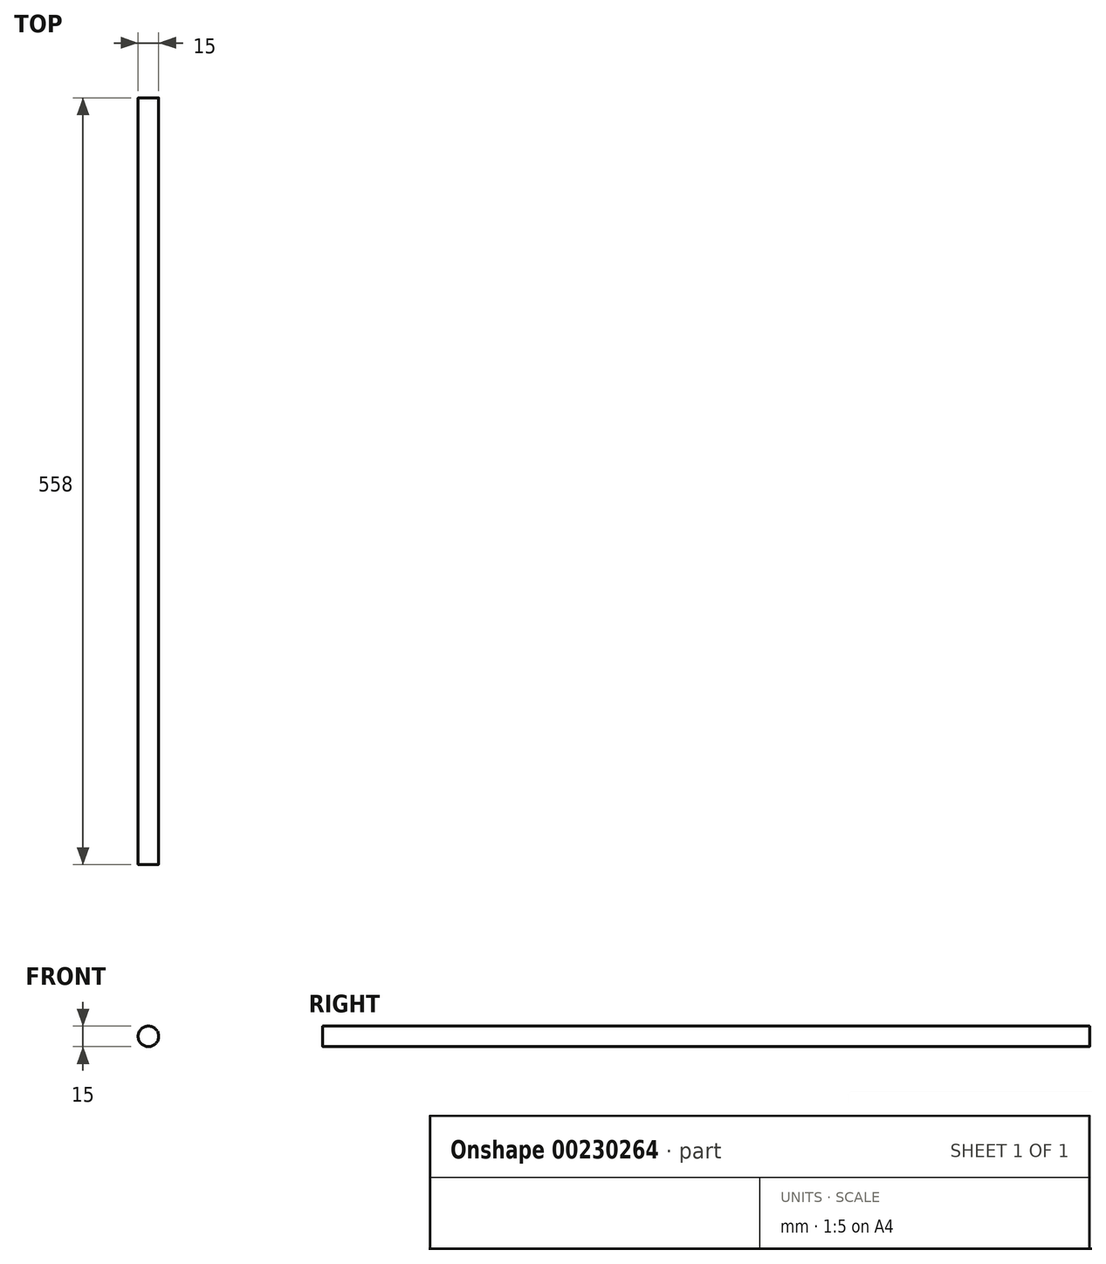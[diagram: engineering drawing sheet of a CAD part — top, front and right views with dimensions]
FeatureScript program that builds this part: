
annotation { "Feature Type Name" : "Feature", "Feature Type Description" : "" }
export const myFeature = defineFeature(function(context is Context, id is Id, definition is map)
    precondition{}
    {
        {
            var Q0;
            Q0=qCreatedBy(makeId("Front.planeOp"),FACE);
            var sketch = newSketch(context, id + "F0", { "sketchPlane" : qUnion([Q0])});
            skCircle(sketch, "E0", {"center": v(0, 0) * mm, "radius": 7.5 * mm});
            skSolve(sketch);
        }
        {
            var Q0;
            Q0=makeQuery(id+"F0.imprint","IMPRINT",FACE,{"disambiguationData":[TD([[makeQuery(id+"F0.imprint","IMPRINT",EDGE,{"derivedFrom":sQuery(id+"F0.wireOp",EDGE,"E0")}),1.0]])]});
            extrude(context, id + "F1", {"entities" : qUnion([Q0]), "endBound" : BoundingType.SYMMETRIC, "depth" : 558 * mm});
        }
        {
            var Q0;
            Q0=makeQuery(id+"F1.opExtrude","CAP_EDGE",EDGE,{"disambiguationData":[OSD([sQuery(id+"F0.wireOp",EDGE,"E0")])],"isStart":false});
            var Q1;
            Q1=makeQuery(id+"F1.opExtrude","CAP_EDGE",EDGE,{"disambiguationData":[OSD([sQuery(id+"F0.wireOp",EDGE,"E0")])],"isStart":true});
            fillet(context, id + "F2", {"entities" : qUnion([Q0, Q1]), "radius" : 0.2 * mm, "tangentPropagation" : true, "allowEdgeOverflow" : false});
        }
    });
